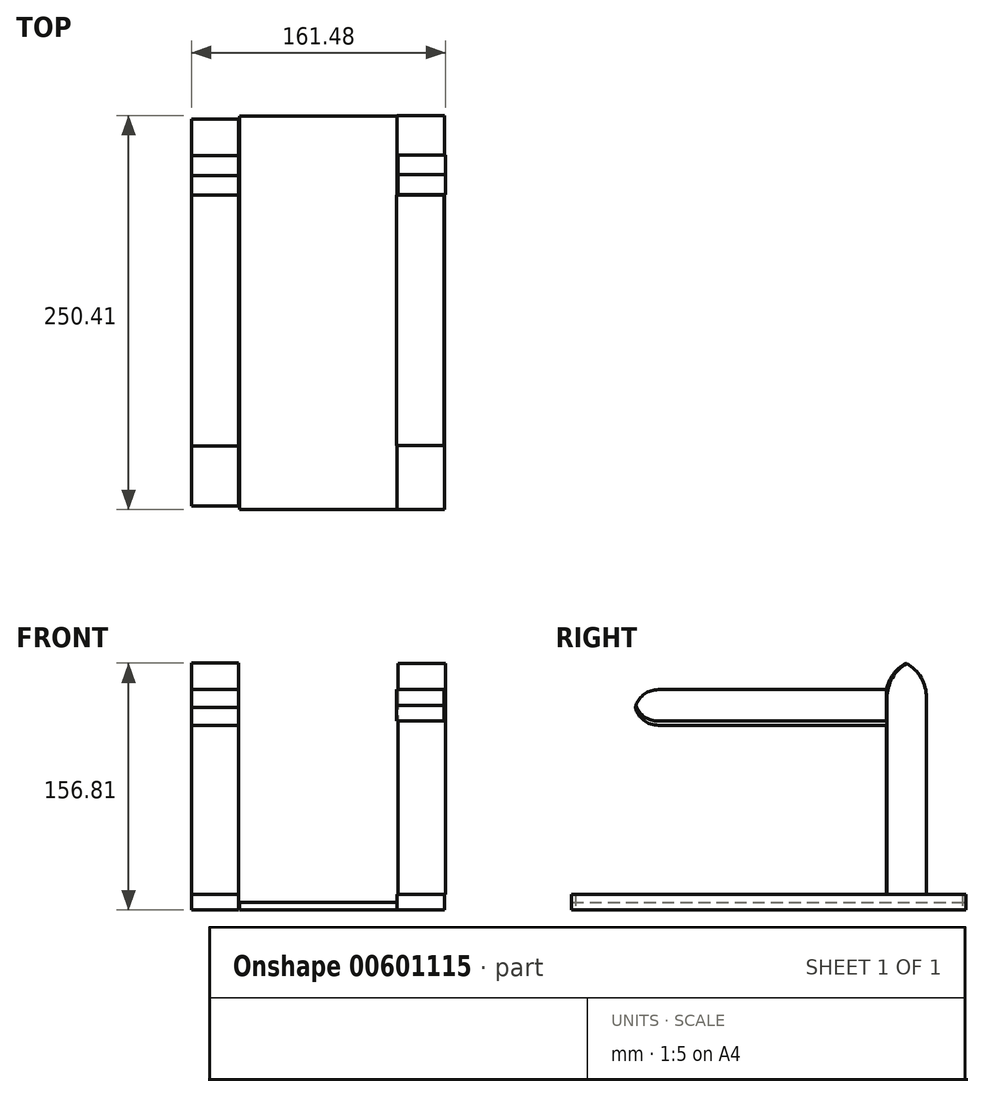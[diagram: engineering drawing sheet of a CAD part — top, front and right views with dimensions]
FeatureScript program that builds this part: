
annotation { "Feature Type Name" : "Feature", "Feature Type Description" : "" }
export const myFeature = defineFeature(function(context is Context, id is Id, definition is map)
    precondition{}
    {
        {
            var Q0;
            Q0=qCreatedBy(makeId("Top.planeOp"),FACE);
            var sketch = newSketch(context, id + "F0", { "sketchPlane" : qUnion([Q0])});
            skLineSegment(sketch, "E0.bottom", {"start": v(-41.16, -63.75) * mm, "end": v(58.84, -63.75) * mm});
            skLineSegment(sketch, "E0.top", {"start": v(-41.16, 186.25) * mm, "end": v(58.84, 186.25) * mm});
            skLineSegment(sketch, "E0.left", {"start": v(-41.16, -63.75) * mm, "end": v(-41.16, 186.25) * mm});
            skLineSegment(sketch, "E0.right", {"start": v(58.84, -63.75) * mm, "end": v(58.84, 186.25) * mm});
            skSolve(sketch);
        }
        {
            var Q0;
            Q0 = qSketchRegion(id + "F0", true);
            extrude(context, id + "F1", {"entities" : qUnion([Q0]), "depth" : 5 * mm, "offsetDistance" : 25 * mm});
        }
        {
            var Q0;
            Q0=qCreatedBy(makeId("Top.planeOp"),FACE);
            var sketch = newSketch(context, id + "F2", { "sketchPlane" : qUnion([Q0])});
            skLineSegment(sketch, "E1.bottom", {"start": v(-41.8, 184.3) * mm, "end": v(-71.8, 184.3) * mm});
            skLineSegment(sketch, "E1.top", {"start": v(-41.8, -61.54) * mm, "end": v(-71.8, -61.54) * mm});
            skLineSegment(sketch, "E1.left", {"start": v(-41.8, 184.3) * mm, "end": v(-41.8, -61.54) * mm});
            skLineSegment(sketch, "E1.right", {"start": v(-71.8, 184.3) * mm, "end": v(-71.8, -61.54) * mm});
            skLineSegment(sketch, "E2.bottom", {"start": v(58.88, 186.6) * mm, "end": v(89.05, 186.6) * mm});
            skLineSegment(sketch, "E2.top", {"start": v(58.88, -63.82) * mm, "end": v(89.05, -63.82) * mm});
            skLineSegment(sketch, "E2.left", {"start": v(58.88, 186.6) * mm, "end": v(58.88, -63.82) * mm});
            skLineSegment(sketch, "E2.right", {"start": v(89.05, 186.6) * mm, "end": v(89.05, -63.82) * mm});
            skSolve(sketch);
        }
        {
            var Q0;
            Q0 = qSketchRegion(id + "F2", true);
            extrude(context, id + "F3", {"entities" : qUnion([Q0]), "depth" : 10 * mm, "offsetDistance" : 25 * mm});
        }
        {
            var Q0;
            Q0=makeQuery(id+"F3.opExtrude","CAP_FACE",FACE,{"disambiguationData":[OSD([sQuery(id+"F2.wireOp",EDGE,"E1.bottom"),sQuery(id+"F2.wireOp",EDGE,"E1.top"),sQuery(id+"F2.wireOp",EDGE,"E1.left"),sQuery(id+"F2.wireOp",EDGE,"E1.right")])],"isStart":false});
            var sketch = newSketch(context, id + "F4", { "sketchPlane" : qUnion([Q0])});
            skLineSegment(sketch, "E3.bottom", {"start": v(-71.8, 161.22) * mm, "end": v(-41.8, 161.22) * mm});
            skLineSegment(sketch, "E3.top", {"start": v(-71.8, 136.16) * mm, "end": v(-41.8, 136.16) * mm});
            skLineSegment(sketch, "E3.left", {"start": v(-71.8, 161.22) * mm, "end": v(-71.8, 136.16) * mm});
            skLineSegment(sketch, "E3.right", {"start": v(-41.8, 161.22) * mm, "end": v(-41.8, 136.16) * mm});
            skLineSegment(sketch, "E4.bottom", {"start": v(59.24, 161.53) * mm, "end": v(89.68, 161.53) * mm});
            skLineSegment(sketch, "E4.top", {"start": v(59.24, 136.48) * mm, "end": v(89.68, 136.48) * mm});
            skLineSegment(sketch, "E4.left", {"start": v(59.24, 161.53) * mm, "end": v(59.24, 136.48) * mm});
            skLineSegment(sketch, "E4.right", {"start": v(89.68, 161.53) * mm, "end": v(89.68, 136.48) * mm});
            skSolve(sketch);
        }
        {
            var Q0;
            Q0=makeQuery(id+"F4.imprint","IMPRINT",FACE,{"disambiguationData":[TD([[makeQuery(id+"F4.imprint","IMPRINT",EDGE,{"derivedFrom":sQuery(id+"F4.wireOp",EDGE,"E3.bottom")}),-1.0]])]});
            var Q1;
            Q1=makeQuery(id+"F4.imprint","IMPRINT",FACE,{"disambiguationData":[TD([[makeQuery(id+"F4.imprint","IMPRINT",EDGE,{"derivedFrom":sQuery(id+"F4.wireOp",EDGE,"E4.bottom")}),-1.0]])]});
            extrude(context, id + "F5", {"entities" : qUnion([Q0, Q1]), "depth" : 150 * mm, "offsetDistance" : 25 * mm});
        }
        {
            var Q0;
            Q0=makeQuery(id+"F5.opExtrude","SWEPT_FACE",FACE,{"disambiguationData":[OSD([sQuery(id+"F4.wireOp",EDGE,"E3.top")])]});
            var sketch = newSketch(context, id + "F6", { "sketchPlane" : qUnion([Q0])});
            skLineSegment(sketch, "E5.bottom", {"start": v(-71.8, 140) * mm, "end": v(-41.8, 140) * mm});
            skLineSegment(sketch, "E5.top", {"start": v(-71.8, 117.4) * mm, "end": v(-41.8, 117.4) * mm});
            skLineSegment(sketch, "E5.left", {"start": v(-71.8, 140) * mm, "end": v(-71.8, 117.4) * mm});
            skLineSegment(sketch, "E5.right", {"start": v(-41.8, 140) * mm, "end": v(-41.8, 117.4) * mm});
            skLineSegment(sketch, "E6.bottom", {"start": v(58.52, 140) * mm, "end": v(88.52, 140) * mm});
            skLineSegment(sketch, "E6.top", {"start": v(58.52, 120) * mm, "end": v(88.52, 120) * mm});
            skLineSegment(sketch, "E6.left", {"start": v(58.52, 140) * mm, "end": v(58.52, 120) * mm});
            skLineSegment(sketch, "E6.right", {"start": v(88.52, 140) * mm, "end": v(88.52, 120) * mm});
            skSolve(sketch);
        }
        {
            var Q0;
            Q0 = qSketchRegion(id + "F6", true);
            extrude(context, id + "F7", {"entities" : qUnion([Q0]), "operationType" : NewBodyOperationType.ADD, "depth" : 160 * mm, "offsetDistance" : 25 * mm});
        }
        {
            var Q0;
            Q0=makeQuery(id+"F5.opExtrude","CAP_EDGE",EDGE,{"disambiguationData":[OSD([sQuery(id+"F4.wireOp",EDGE,"E3.top")])],"isStart":false});
            var Q1;
            Q1=makeQuery(id+"F5.opExtrude","CAP_EDGE",EDGE,{"disambiguationData":[OSD([sQuery(id+"F4.wireOp",EDGE,"E3.bottom")])],"isStart":false});
            var Q2;
            Q2=makeQuery(id+"F5.opExtrude","CAP_EDGE",EDGE,{"disambiguationData":[OSD([sQuery(id+"F4.wireOp",EDGE,"E4.top")])],"isStart":false});
            var Q3;
            Q3=makeQuery(id+"F5.opExtrude","CAP_EDGE",EDGE,{"disambiguationData":[OSD([sQuery(id+"F4.wireOp",EDGE,"E4.bottom")])],"isStart":false});
            fillet(context, id + "F8", {"entities" : qUnion([Q0, Q1, Q2, Q3]), "radius" : 25 * mm, "tangentPropagation" : true, "allowEdgeOverflow" : false});
        }
        {
            var Q0;
            Q0=makeQuery(id+"F7.opExtrude","CAP_EDGE",EDGE,{"disambiguationData":[OSD([sQuery(id+"F6.wireOp",EDGE,"E5.bottom")])],"isStart":false});
            var Q1;
            Q1=makeQuery(id+"F7.opExtrude","CAP_EDGE",EDGE,{"disambiguationData":[OSD([sQuery(id+"F6.wireOp",EDGE,"E5.top")])],"isStart":false});
            var Q2;
            Q2=makeQuery(id+"F7.opExtrude","CAP_EDGE",EDGE,{"disambiguationData":[OSD([sQuery(id+"F6.wireOp",EDGE,"E6.bottom")])],"isStart":false});
            var Q3;
            Q3=makeQuery(id+"F7.opExtrude","CAP_EDGE",EDGE,{"disambiguationData":[OSD([sQuery(id+"F6.wireOp",EDGE,"E6.top")])],"isStart":false});
            fillet(context, id + "F9", {"entities" : qUnion([Q0, Q1, Q2, Q3]), "radius" : 15 * mm, "tangentPropagation" : true, "allowEdgeOverflow" : false});
        }
    });
